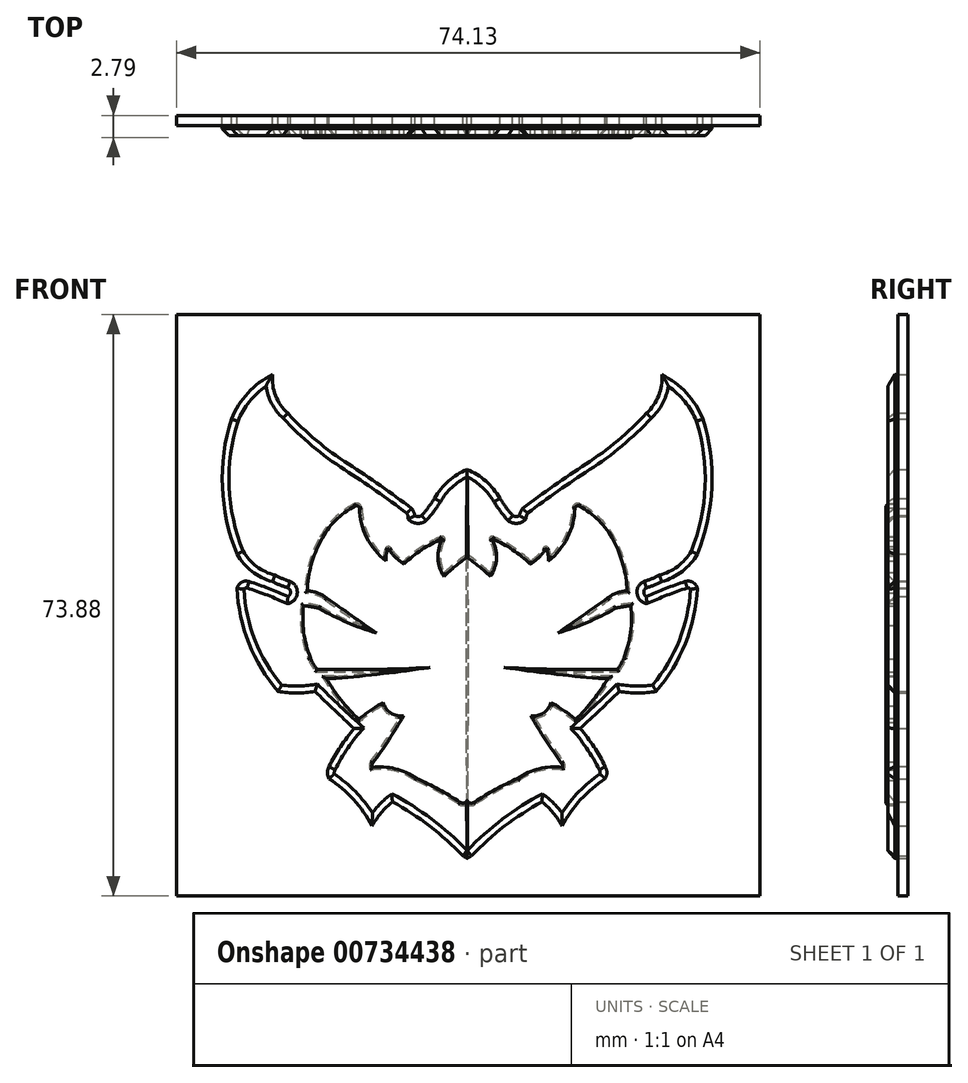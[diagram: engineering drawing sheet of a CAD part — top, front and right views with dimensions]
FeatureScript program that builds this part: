
annotation { "Feature Type Name" : "Feature", "Feature Type Description" : "" }
export const myFeature = defineFeature(function(context is Context, id is Id, definition is map)
    precondition{}
    {
        {
            var Q0;
            Q0=qCreatedBy(makeId("Front.planeOp"),FACE);
            var sketch = newSketch(context, id + "F0", { "sketchPlane" : qUnion([Q0])});
            skArc(sketch, "E0", {"start": v(0, 21.15) * mm, "mid": v(-2.37, 19.64) * mm, "end": v(-4.15, 17.47) * mm});
            skArc(sketch, "E1", {"start": v(-5.78, 15.28) * mm, "mid": v(-4.92, 16.34) * mm, "end": v(-4.15, 17.47) * mm});
            skArc(sketch, "E2", {"start": v(-6.65, 15.28) * mm, "mid": v(-6.22, 15.15) * mm, "end": v(-5.78, 15.28) * mm});
            skArc(sketch, "E3", {"start": v(-6.65, 15.28) * mm, "mid": v(-6.8, 15.75) * mm, "end": v(-7.04, 16.18) * mm});
            skArc(sketch, "E4", {"start": v(-7.04, 16.18) * mm, "mid": v(-11.01, 19.07) * mm, "end": v(-15.08, 21.83) * mm});
            skArc(sketch, "E5", {"start": v(-22.78, 28.28) * mm, "mid": v(-19.14, 24.8) * mm, "end": v(-15.08, 21.83) * mm});
            skArc(sketch, "E6", {"start": v(-24.73, 33.18) * mm, "mid": v(-24.33, 30.5) * mm, "end": v(-22.78, 28.28) * mm});
            skArc(sketch, "E7", {"start": v(-24.73, 33.18) * mm, "mid": v(-27.86, 30.85) * mm, "end": v(-29.94, 27.55) * mm});
            skArc(sketch, "E8", {"start": v(-29.94, 27.55) * mm, "mid": v(-31.1, 18.9) * mm, "end": v(-29.24, 10.37) * mm});
            skArc(sketch, "E9", {"start": v(-29.24, 10.37) * mm, "mid": v(-27.33, 8.18) * mm, "end": v(-24.73, 6.9) * mm});
            skArc(sketch, "E10", {"start": v(-24.73, 6.9) * mm, "mid": v(-23.77, 6.45) * mm, "end": v(-22.78, 6.1) * mm});
            skArc(sketch, "E11", {"start": v(-22.78, 5) * mm, "mid": v(-22.43, 5.55) * mm, "end": v(-22.78, 6.1) * mm});
            skArc(sketch, "E12", {"start": v(-22.78, 5) * mm, "mid": v(-25.2, 6.02) * mm, "end": v(-27.7, 6.9) * mm});
            skArc(sketch, "E13", {"start": v(-27.7, 6.9) * mm, "mid": v(-28.66, 6.8) * mm, "end": v(-29.24, 6.02) * mm});
            skPoint(sketch, "E13.endSnap0", {"position": v(-25.2, 6.02) * mm});
            skArc(sketch, "E14", {"start": v(-29.24, 6.02) * mm, "mid": v(-27.72, -0.96) * mm, "end": v(-24, -7.06) * mm});
            skArc(sketch, "E15", {"start": v(-24, -7.06) * mm, "mid": v(-21.67, -7.26) * mm, "end": v(-19.32, -7.06) * mm});
            skArc(sketch, "E16", {"start": v(-19.32, -7.06) * mm, "mid": v(-16.86, -9.44) * mm, "end": v(-14.34, -11.77) * mm});
            skArc(sketch, "E17", {"start": v(-14.34, -11.77) * mm, "mid": v(-16.1, -14.1) * mm, "end": v(-17.53, -16.62) * mm});
            skArc(sketch, "E18", {"start": v(-17.53, -16.62) * mm, "mid": v(-17.75, -17.38) * mm, "end": v(-17.53, -18.15) * mm});
            skArc(sketch, "E19", {"start": v(-12.06, -24.15) * mm, "mid": v(-14.43, -20.8) * mm, "end": v(-17.53, -18.15) * mm});
            skArc(sketch, "E20", {"start": v(-9.5, -21.1) * mm, "mid": v(-10.93, -22.5) * mm, "end": v(-12.06, -24.15) * mm});
            skArc(sketch, "E21", {"start": v(-0.55, -27.97) * mm, "mid": v(-4.75, -24.18) * mm, "end": v(-9.5, -21.1) * mm});
            skArc(sketch, "E22", {"start": v(0, -28.27) * mm, "mid": v(-0.27, -28.11) * mm, "end": v(-0.55, -27.97) * mm});
            skArc(sketch, "E23", {"start": v(0, 21.15) * mm, "mid": v(-0.15, -3.56) * mm, "end": v(0, -28.27) * mm});
            skSolve(sketch);
        }
        {
            var Q0;
            Q0 = qSketchRegion(id + "F0", true);
            extrude(context, id + "F1", {"entities" : qUnion([Q0]), "depth" : 2.54 * mm, "offsetDistance" : 25.4 * mm});
        }
        {
            var Q0;
            Q0=makeQuery(id+"F1.opExtrude","SWEPT_BODY",BODY,{"disambiguationData":[OSD([sQuery(id+"F0.wireOp",EDGE,"E0"),sQuery(id+"F0.wireOp",EDGE,"E1"),sQuery(id+"F0.wireOp",EDGE,"E2"),sQuery(id+"F0.wireOp",EDGE,"E3"),sQuery(id+"F0.wireOp",EDGE,"E4"),sQuery(id+"F0.wireOp",EDGE,"E5"),sQuery(id+"F0.wireOp",EDGE,"E6"),sQuery(id+"F0.wireOp",EDGE,"E7"),sQuery(id+"F0.wireOp",EDGE,"E8"),sQuery(id+"F0.wireOp",EDGE,"E9"),sQuery(id+"F0.wireOp",EDGE,"E10"),sQuery(id+"F0.wireOp",EDGE,"E11"),sQuery(id+"F0.wireOp",EDGE,"E12"),sQuery(id+"F0.wireOp",EDGE,"E13"),sQuery(id+"F0.wireOp",EDGE,"E14"),sQuery(id+"F0.wireOp",EDGE,"E15"),sQuery(id+"F0.wireOp",EDGE,"E16"),sQuery(id+"F0.wireOp",EDGE,"E17"),sQuery(id+"F0.wireOp",EDGE,"E18"),sQuery(id+"F0.wireOp",EDGE,"E19"),sQuery(id+"F0.wireOp",EDGE,"E20"),sQuery(id+"F0.wireOp",EDGE,"E21"),sQuery(id+"F0.wireOp",EDGE,"E22"),sQuery(id+"F0.wireOp",EDGE,"E23")])]});
            var Q1;
            Q1=qCreatedBy(makeId("Right.planeOp"),FACE);
            mirror(context, id + "F2", {"entities" : qUnion([Q0]), "mirrorPlane" : qUnion([Q1])});
        }
        {
            var Q0;
            Q0=qCreatedBy(makeId("Front.planeOp"),FACE);
            var sketch = newSketch(context, id + "F3", { "sketchPlane" : qUnion([Q0])});
            skLineSegment(sketch, "E24.bottom", {"start": v(-36.94, 40.82) * mm, "end": v(37.19, 40.82) * mm});
            skLineSegment(sketch, "E24.top", {"start": v(-36.94, -33.06) * mm, "end": v(37.19, -33.06) * mm});
            skLineSegment(sketch, "E24.left", {"start": v(-36.94, 40.82) * mm, "end": v(-36.94, -33.06) * mm});
            skLineSegment(sketch, "E24.right", {"start": v(37.19, 40.82) * mm, "end": v(37.19, -33.06) * mm});
            skSolve(sketch);
        }
        {
            var Q0;
            Q0 = qSketchRegion(id + "F3", true);
            extrude(context, id + "F4", {"entities" : qUnion([Q0]), "depth" : 1.27 * mm, "offsetDistance" : 25.4 * mm});
        }
        {
            var Q0;
            Q0=makeQuery(id+"F1.opExtrude","CAP_EDGE",EDGE,{"disambiguationData":[OSD([sQuery(id+"F0.wireOp",EDGE,"E4")])],"isStart":false});
            var Q1;
            Q1=makeQuery(id+"F1.opExtrude","CAP_EDGE",EDGE,{"disambiguationData":[OSD([sQuery(id+"F0.wireOp",EDGE,"E5")])],"isStart":false});
            var Q2;
            Q2=makeQuery(id+"F1.opExtrude","CAP_EDGE",EDGE,{"disambiguationData":[OSD([sQuery(id+"F0.wireOp",EDGE,"E6")])],"isStart":false});
            var Q3;
            Q3=makeQuery(id+"F1.opExtrude","CAP_EDGE",EDGE,{"disambiguationData":[OSD([sQuery(id+"F0.wireOp",EDGE,"E3")])],"isStart":false});
            var Q4;
            Q4=makeQuery(id+"F1.opExtrude","CAP_EDGE",EDGE,{"disambiguationData":[OSD([sQuery(id+"F0.wireOp",EDGE,"E2")])],"isStart":false});
            var Q5;
            Q5=makeQuery(id+"F1.opExtrude","CAP_EDGE",EDGE,{"disambiguationData":[OSD([sQuery(id+"F0.wireOp",EDGE,"E1")])],"isStart":false});
            var Q6;
            Q6=makeQuery(id+"F1.opExtrude","CAP_EDGE",EDGE,{"disambiguationData":[OSD([sQuery(id+"F0.wireOp",EDGE,"E0")])],"isStart":false});
            var Q7;
            Q7=makeQuery(id+"F2.opPattern","COPY",EDGE,{"derivedFrom":makeQuery(id+"F1.opExtrude","CAP_EDGE",EDGE,{"disambiguationData":[OSD([sQuery(id+"F0.wireOp",EDGE,"E0")])],"isStart":false}),"instanceName":"1"});
            var Q8;
            Q8=makeQuery(id+"F2.opPattern","COPY",EDGE,{"derivedFrom":makeQuery(id+"F1.opExtrude","CAP_EDGE",EDGE,{"disambiguationData":[OSD([sQuery(id+"F0.wireOp",EDGE,"E1")])],"isStart":false}),"instanceName":"1"});
            var Q9;
            Q9=makeQuery(id+"F2.opPattern","COPY",EDGE,{"derivedFrom":makeQuery(id+"F1.opExtrude","CAP_EDGE",EDGE,{"disambiguationData":[OSD([sQuery(id+"F0.wireOp",EDGE,"E2")])],"isStart":false}),"instanceName":"1"});
            var Q10;
            Q10=makeQuery(id+"F2.opPattern","COPY",EDGE,{"derivedFrom":makeQuery(id+"F1.opExtrude","CAP_EDGE",EDGE,{"disambiguationData":[OSD([sQuery(id+"F0.wireOp",EDGE,"E3")])],"isStart":false}),"instanceName":"1"});
            var Q11;
            Q11=makeQuery(id+"F2.opPattern","COPY",EDGE,{"derivedFrom":makeQuery(id+"F1.opExtrude","CAP_EDGE",EDGE,{"disambiguationData":[OSD([sQuery(id+"F0.wireOp",EDGE,"E4")])],"isStart":false}),"instanceName":"1"});
            var Q12;
            Q12=makeQuery(id+"F2.opPattern","COPY",EDGE,{"derivedFrom":makeQuery(id+"F1.opExtrude","CAP_EDGE",EDGE,{"disambiguationData":[OSD([sQuery(id+"F0.wireOp",EDGE,"E5")])],"isStart":false}),"instanceName":"1"});
            var Q13;
            Q13=makeQuery(id+"F2.opPattern","COPY",EDGE,{"derivedFrom":makeQuery(id+"F1.opExtrude","CAP_EDGE",EDGE,{"disambiguationData":[OSD([sQuery(id+"F0.wireOp",EDGE,"E6")])],"isStart":false}),"instanceName":"1"});
            var Q14;
            Q14=makeQuery(id+"F2.opPattern","COPY",EDGE,{"derivedFrom":makeQuery(id+"F1.opExtrude","CAP_EDGE",EDGE,{"disambiguationData":[OSD([sQuery(id+"F0.wireOp",EDGE,"E7")])],"isStart":false}),"instanceName":"1"});
            var Q15;
            Q15=makeQuery(id+"F2.opPattern","COPY",EDGE,{"derivedFrom":makeQuery(id+"F1.opExtrude","CAP_EDGE",EDGE,{"disambiguationData":[OSD([sQuery(id+"F0.wireOp",EDGE,"E8")])],"isStart":false}),"instanceName":"1"});
            var Q16;
            Q16=makeQuery(id+"F2.opPattern","COPY",EDGE,{"derivedFrom":makeQuery(id+"F1.opExtrude","CAP_EDGE",EDGE,{"disambiguationData":[OSD([sQuery(id+"F0.wireOp",EDGE,"E9")])],"isStart":false}),"instanceName":"1"});
            var Q17;
            Q17=makeQuery(id+"F2.opPattern","COPY",EDGE,{"derivedFrom":makeQuery(id+"F1.opExtrude","CAP_EDGE",EDGE,{"disambiguationData":[OSD([sQuery(id+"F0.wireOp",EDGE,"E10")])],"isStart":false}),"instanceName":"1"});
            var Q18;
            Q18=makeQuery(id+"F2.opPattern","COPY",EDGE,{"derivedFrom":makeQuery(id+"F1.opExtrude","CAP_EDGE",EDGE,{"disambiguationData":[OSD([sQuery(id+"F0.wireOp",EDGE,"E11")])],"isStart":false}),"instanceName":"1"});
            var Q19;
            Q19=makeQuery(id+"F2.opPattern","COPY",EDGE,{"derivedFrom":makeQuery(id+"F1.opExtrude","CAP_EDGE",EDGE,{"disambiguationData":[OSD([sQuery(id+"F0.wireOp",EDGE,"E12")])],"isStart":false}),"instanceName":"1"});
            var Q20;
            Q20=makeQuery(id+"F2.opPattern","COPY",EDGE,{"derivedFrom":makeQuery(id+"F1.opExtrude","CAP_EDGE",EDGE,{"disambiguationData":[OSD([sQuery(id+"F0.wireOp",EDGE,"E13")])],"isStart":false}),"instanceName":"1"});
            var Q21;
            Q21=makeQuery(id+"F2.opPattern","COPY",EDGE,{"derivedFrom":makeQuery(id+"F1.opExtrude","CAP_EDGE",EDGE,{"disambiguationData":[OSD([sQuery(id+"F0.wireOp",EDGE,"E14")])],"isStart":false}),"instanceName":"1"});
            var Q22;
            Q22=makeQuery(id+"F2.opPattern","COPY",EDGE,{"derivedFrom":makeQuery(id+"F1.opExtrude","CAP_EDGE",EDGE,{"disambiguationData":[OSD([sQuery(id+"F0.wireOp",EDGE,"E15")])],"isStart":false}),"instanceName":"1"});
            var Q23;
            Q23=makeQuery(id+"F2.opPattern","COPY",EDGE,{"derivedFrom":makeQuery(id+"F1.opExtrude","CAP_EDGE",EDGE,{"disambiguationData":[OSD([sQuery(id+"F0.wireOp",EDGE,"E16")])],"isStart":false}),"instanceName":"1"});
            var Q24;
            Q24=makeQuery(id+"F2.opPattern","COPY",EDGE,{"derivedFrom":makeQuery(id+"F1.opExtrude","CAP_EDGE",EDGE,{"disambiguationData":[OSD([sQuery(id+"F0.wireOp",EDGE,"E17")])],"isStart":false}),"instanceName":"1"});
            var Q25;
            Q25=makeQuery(id+"F2.opPattern","COPY",EDGE,{"derivedFrom":makeQuery(id+"F1.opExtrude","CAP_EDGE",EDGE,{"disambiguationData":[OSD([sQuery(id+"F0.wireOp",EDGE,"E18")])],"isStart":false}),"instanceName":"1"});
            var Q26;
            Q26=makeQuery(id+"F2.opPattern","COPY",EDGE,{"derivedFrom":makeQuery(id+"F1.opExtrude","CAP_EDGE",EDGE,{"disambiguationData":[OSD([sQuery(id+"F0.wireOp",EDGE,"E19")])],"isStart":false}),"instanceName":"1"});
            var Q27;
            Q27=makeQuery(id+"F2.opPattern","COPY",EDGE,{"derivedFrom":makeQuery(id+"F1.opExtrude","CAP_EDGE",EDGE,{"disambiguationData":[OSD([sQuery(id+"F0.wireOp",EDGE,"E20")])],"isStart":false}),"instanceName":"1"});
            var Q28;
            Q28=makeQuery(id+"F2.opPattern","COPY",EDGE,{"derivedFrom":makeQuery(id+"F1.opExtrude","CAP_EDGE",EDGE,{"disambiguationData":[OSD([sQuery(id+"F0.wireOp",EDGE,"E21")])],"isStart":false}),"instanceName":"1"});
            var Q29;
            Q29=makeQuery(id+"F2.opPattern","COPY",EDGE,{"derivedFrom":makeQuery(id+"F1.opExtrude","CAP_EDGE",EDGE,{"disambiguationData":[OSD([sQuery(id+"F0.wireOp",EDGE,"E22")])],"isStart":false}),"instanceName":"1"});
            var Q30;
            Q30=makeQuery(id+"F1.opExtrude","CAP_EDGE",EDGE,{"disambiguationData":[OSD([sQuery(id+"F0.wireOp",EDGE,"E22")])],"isStart":false});
            var Q31;
            Q31=makeQuery(id+"F1.opExtrude","CAP_EDGE",EDGE,{"disambiguationData":[OSD([sQuery(id+"F0.wireOp",EDGE,"E21")])],"isStart":false});
            var Q32;
            Q32=makeQuery(id+"F1.opExtrude","CAP_EDGE",EDGE,{"disambiguationData":[OSD([sQuery(id+"F0.wireOp",EDGE,"E20")])],"isStart":false});
            var Q33;
            Q33=makeQuery(id+"F1.opExtrude","CAP_EDGE",EDGE,{"disambiguationData":[OSD([sQuery(id+"F0.wireOp",EDGE,"E19")])],"isStart":false});
            var Q34;
            Q34=makeQuery(id+"F1.opExtrude","CAP_EDGE",EDGE,{"disambiguationData":[OSD([sQuery(id+"F0.wireOp",EDGE,"E18")])],"isStart":false});
            var Q35;
            Q35=makeQuery(id+"F1.opExtrude","CAP_EDGE",EDGE,{"disambiguationData":[OSD([sQuery(id+"F0.wireOp",EDGE,"E17")])],"isStart":false});
            var Q36;
            Q36=makeQuery(id+"F1.opExtrude","CAP_EDGE",EDGE,{"disambiguationData":[OSD([sQuery(id+"F0.wireOp",EDGE,"E16")])],"isStart":false});
            var Q37;
            Q37=makeQuery(id+"F1.opExtrude","CAP_EDGE",EDGE,{"disambiguationData":[OSD([sQuery(id+"F0.wireOp",EDGE,"E15")])],"isStart":false});
            var Q38;
            Q38=makeQuery(id+"F1.opExtrude","CAP_EDGE",EDGE,{"disambiguationData":[OSD([sQuery(id+"F0.wireOp",EDGE,"E14")])],"isStart":false});
            var Q39;
            Q39=makeQuery(id+"F1.opExtrude","CAP_EDGE",EDGE,{"disambiguationData":[OSD([sQuery(id+"F0.wireOp",EDGE,"E13")])],"isStart":false});
            var Q40;
            Q40=makeQuery(id+"F1.opExtrude","CAP_EDGE",EDGE,{"disambiguationData":[OSD([sQuery(id+"F0.wireOp",EDGE,"E12")])],"isStart":false});
            var Q41;
            Q41=makeQuery(id+"F1.opExtrude","CAP_EDGE",EDGE,{"disambiguationData":[OSD([sQuery(id+"F0.wireOp",EDGE,"E11")])],"isStart":false});
            var Q42;
            Q42=makeQuery(id+"F1.opExtrude","CAP_EDGE",EDGE,{"disambiguationData":[OSD([sQuery(id+"F0.wireOp",EDGE,"E10")])],"isStart":false});
            var Q43;
            Q43=makeQuery(id+"F1.opExtrude","CAP_EDGE",EDGE,{"disambiguationData":[OSD([sQuery(id+"F0.wireOp",EDGE,"E9")])],"isStart":false});
            var Q44;
            Q44=makeQuery(id+"F1.opExtrude","CAP_EDGE",EDGE,{"disambiguationData":[OSD([sQuery(id+"F0.wireOp",EDGE,"E8")])],"isStart":false});
            var Q45;
            Q45=makeQuery(id+"F1.opExtrude","CAP_EDGE",EDGE,{"disambiguationData":[OSD([sQuery(id+"F0.wireOp",EDGE,"E7")])],"isStart":false});
            chamfer(context, id + "F5", {"entities" : qUnion([Q0, Q1, Q2, Q3, Q4, Q5, Q6, Q7, Q8, Q9, Q10, Q11, Q12, Q13, Q14, Q15, Q16, Q17, Q18, Q19, Q20, Q21, Q22, Q23, Q24, Q25, Q26, Q27, Q28, Q29, Q30, Q31, Q32, Q33, Q34, Q35, Q36, Q37, Q38, Q39, Q40, Q41, Q42, Q43, Q44, Q45]), "width" : 0.86 * mm, "tangentPropagation" : true});
        }
        {
            var Q0;
            Q0=makeQuery(id+"F4.opExtrude","CAP_FACE",FACE,{"disambiguationData":[OSD([sQuery(id+"F3.wireOp",EDGE,"E24.bottom"),sQuery(id+"F3.wireOp",EDGE,"E24.top"),sQuery(id+"F3.wireOp",EDGE,"E24.left"),sQuery(id+"F3.wireOp",EDGE,"E24.right")])],"isStart":false});
            var sketch = newSketch(context, id + "F6", { "sketchPlane" : qUnion([Q0])});
            skArc(sketch, "E25", {"start": v(0, 10.33) * mm, "mid": v(-1.49, 9.24) * mm, "end": v(-2.88, 8.03) * mm});
            skArc(sketch, "E26", {"start": v(-2.88, 12.09) * mm, "mid": v(-3.42, 10.06) * mm, "end": v(-2.88, 8.03) * mm});
            skArc(sketch, "E27", {"start": v(-2.88, 12.09) * mm, "mid": v(-2.95, 12.56) * mm, "end": v(-3.42, 12.56) * mm});
            skPoint(sketch, "E27.endSnap0", {"position": v(-3.42, 10.06) * mm});
            skArc(sketch, "E28", {"start": v(-3.42, 12.56) * mm, "mid": v(-5.87, 11.24) * mm, "end": v(-8.05, 9.5) * mm});
            skArc(sketch, "E29", {"start": v(-9.61, 11.03) * mm, "mid": v(-8.9, 10.2) * mm, "end": v(-8.05, 9.5) * mm});
            skArc(sketch, "E30", {"start": v(-9.61, 11.03) * mm, "mid": v(-10, 11.33) * mm, "end": v(-10.4, 11.03) * mm});
            skArc(sketch, "E31", {"start": v(-10.4, 11.03) * mm, "mid": v(-10.53, 10.6) * mm, "end": v(-10.61, 10.16) * mm});
            skArc(sketch, "E32", {"start": v(-13.38, 16.22) * mm, "mid": v(-12.62, 12.9) * mm, "end": v(-10.61, 10.16) * mm});
            skArc(sketch, "E33", {"start": v(-13.38, 16.22) * mm, "mid": v(-13.73, 16.75) * mm, "end": v(-14.36, 16.76) * mm});
            skArc(sketch, "E34", {"start": v(-14.36, 16.76) * mm, "mid": v(-16.95, 14.86) * mm, "end": v(-18.86, 12.26) * mm});
            skArc(sketch, "E35", {"start": v(-18.86, 12.26) * mm, "mid": v(-20.14, 8.94) * mm, "end": v(-20.62, 5.42) * mm});
            skArc(sketch, "E36", {"start": v(-18.02, 4.55) * mm, "mid": v(-19.25, 5.2) * mm, "end": v(-20.62, 5.42) * mm});
            skArc(sketch, "E37", {"start": v(-18.02, 4.55) * mm, "mid": v(-15.7, 2.92) * mm, "end": v(-13.38, 1.3) * mm});
            skArc(sketch, "E38", {"start": v(-18.69, 3.77) * mm, "mid": v(-16.09, 2.41) * mm, "end": v(-13.38, 1.3) * mm});
            skArc(sketch, "E39", {"start": v(-18.69, 3.77) * mm, "mid": v(-19.86, 4.02) * mm, "end": v(-21.05, 4.14) * mm});
            skArc(sketch, "E40", {"start": v(-21.05, 4.14) * mm, "mid": v(-21.08, 0.55) * mm, "end": v(-20.19, -2.92) * mm});
            skArc(sketch, "E41", {"start": v(-20.19, -2.92) * mm, "mid": v(-19.78, -3.78) * mm, "end": v(-19.24, -4.56) * mm});
            skArc(sketch, "E42", {"start": v(-19.24, -4.56) * mm, "mid": v(-15.22, -4.6) * mm, "end": v(-11.2, -4.56) * mm});
            skArc(sketch, "E43", {"start": v(-16.67, -5.14) * mm, "mid": v(-13.94, -4.86) * mm, "end": v(-11.2, -4.56) * mm});
            skArc(sketch, "E44", {"start": v(-16.67, -5.14) * mm, "mid": v(-17.55, -5.1) * mm, "end": v(-18.44, -5.14) * mm});
            skArc(sketch, "E45", {"start": v(-18.44, -5.14) * mm, "mid": v(-16.32, -8.24) * mm, "end": v(-13.8, -11.02) * mm});
            skArc(sketch, "E46", {"start": v(-10.83, -8.9) * mm, "mid": v(-12.35, -9.9) * mm, "end": v(-13.8, -11.02) * mm});
            skArc(sketch, "E47", {"start": v(-10.83, -8.9) * mm, "mid": v(-9.94, -10) * mm, "end": v(-8.61, -10.48) * mm});
            skArc(sketch, "E48", {"start": v(-12.26, -16) * mm, "mid": v(-10.36, -13.29) * mm, "end": v(-8.61, -10.48) * mm});
            skArc(sketch, "E49", {"start": v(-12.26, -16) * mm, "mid": v(-12.43, -16.53) * mm, "end": v(-12.26, -17.06) * mm});
            skArc(sketch, "E50", {"start": v(-6.62, -18.37) * mm, "mid": v(-9.3, -17.15) * mm, "end": v(-12.26, -17.06) * mm});
            skArc(sketch, "E51", {"start": v(-1.07, -21.38) * mm, "mid": v(-3.79, -19.78) * mm, "end": v(-6.62, -18.37) * mm});
            skArc(sketch, "E52", {"start": v(-1.07, -21.38) * mm, "mid": v(-0.54, -21.57) * mm, "end": v(0, -21.38) * mm});
            skArc(sketch, "E53", {"start": v(0, 10.33) * mm, "mid": v(-0.06, -5.53) * mm, "end": v(0, -21.38) * mm});
            skArc(sketch, "E54.MirrorCS", {"start": v(10.4, 11.03) * mm, "mid": v(10.53, 10.6) * mm, "end": v(10.61, 10.16) * mm});
            skArc(sketch, "E55.MirrorCS", {"start": v(2.88, 12.09) * mm, "mid": v(2.95, 12.56) * mm, "end": v(3.42, 12.56) * mm});
            skArc(sketch, "E56.MirrorCS", {"start": v(9.61, 11.03) * mm, "mid": v(10, 11.33) * mm, "end": v(10.4, 11.03) * mm});
            skArc(sketch, "E57.MirrorCS", {"start": v(18.69, 3.77) * mm, "mid": v(19.86, 4.02) * mm, "end": v(21.05, 4.14) * mm});
            skArc(sketch, "E58.MirrorCS", {"start": v(16.67, -5.14) * mm, "mid": v(17.55, -5.1) * mm, "end": v(18.44, -5.14) * mm});
            skArc(sketch, "E59.MirrorCS", {"start": v(10.83, -8.9) * mm, "mid": v(12.35, -9.9) * mm, "end": v(13.8, -11.02) * mm});
            skArc(sketch, "E60.MirrorCS", {"start": v(18.02, 4.55) * mm, "mid": v(19.25, 5.2) * mm, "end": v(20.62, 5.42) * mm});
            skArc(sketch, "E61.MirrorCS", {"start": v(20.19, -2.92) * mm, "mid": v(19.78, -3.78) * mm, "end": v(19.24, -4.56) * mm});
            skArc(sketch, "E62.MirrorCS", {"start": v(12.26, -16) * mm, "mid": v(12.43, -16.53) * mm, "end": v(12.26, -17.06) * mm});
            skArc(sketch, "E63.MirrorCS", {"start": v(1.07, -21.38) * mm, "mid": v(0.54, -21.57) * mm, "end": v(0, -21.38) * mm});
            skArc(sketch, "E64.MirrorCS", {"start": v(13.38, 16.22) * mm, "mid": v(13.73, 16.75) * mm, "end": v(14.36, 16.76) * mm});
            skArc(sketch, "E65.MirrorCS", {"start": v(9.61, 11.03) * mm, "mid": v(8.9, 10.2) * mm, "end": v(8.05, 9.5) * mm});
            skArc(sketch, "E66.MirrorCS", {"start": v(10.83, -8.9) * mm, "mid": v(9.94, -10) * mm, "end": v(8.61, -10.48) * mm});
            skArc(sketch, "E67.MirrorCS", {"start": v(2.88, 12.09) * mm, "mid": v(3.42, 10.06) * mm, "end": v(2.88, 8.03) * mm});
            skArc(sketch, "E68.MirrorCS", {"start": v(1.07, -21.38) * mm, "mid": v(3.79, -19.78) * mm, "end": v(6.62, -18.37) * mm});
            skArc(sketch, "E69.MirrorCS", {"start": v(18.69, 3.77) * mm, "mid": v(16.09, 2.41) * mm, "end": v(13.38, 1.3) * mm});
            skArc(sketch, "E70.MirrorCS", {"start": v(21.05, 4.14) * mm, "mid": v(21.08, 0.55) * mm, "end": v(20.19, -2.92) * mm});
            skArc(sketch, "E71.MirrorCS", {"start": v(6.62, -18.37) * mm, "mid": v(9.3, -17.15) * mm, "end": v(12.26, -17.06) * mm});
            skArc(sketch, "E72.MirrorCS", {"start": v(0, 10.33) * mm, "mid": v(1.49, 9.24) * mm, "end": v(2.88, 8.03) * mm});
            skArc(sketch, "E73.MirrorCS", {"start": v(18.02, 4.55) * mm, "mid": v(15.7, 2.92) * mm, "end": v(13.38, 1.3) * mm});
            skPoint(sketch, "E74.MirrorP", {"position": v(3.42, 10.06) * mm});
            skArc(sketch, "E75.MirrorCS", {"start": v(18.86, 12.26) * mm, "mid": v(20.14, 8.94) * mm, "end": v(20.62, 5.42) * mm});
            skArc(sketch, "E76.MirrorCS", {"start": v(0, 10.33) * mm, "mid": v(0.06, -5.53) * mm, "end": v(0, -21.38) * mm});
            skArc(sketch, "E77.MirrorCS", {"start": v(13.38, 16.22) * mm, "mid": v(12.62, 12.9) * mm, "end": v(10.61, 10.16) * mm});
            skArc(sketch, "E78.MirrorCS", {"start": v(19.24, -4.56) * mm, "mid": v(15.22, -4.6) * mm, "end": v(11.2, -4.56) * mm});
            skArc(sketch, "E79.MirrorCS", {"start": v(3.42, 12.56) * mm, "mid": v(5.87, 11.24) * mm, "end": v(8.05, 9.5) * mm});
            skArc(sketch, "E80.MirrorCS", {"start": v(14.36, 16.76) * mm, "mid": v(16.95, 14.86) * mm, "end": v(18.86, 12.26) * mm});
            skArc(sketch, "E81.MirrorCS", {"start": v(12.26, -16) * mm, "mid": v(10.36, -13.29) * mm, "end": v(8.61, -10.48) * mm});
            skArc(sketch, "E82.MirrorCS", {"start": v(16.67, -5.14) * mm, "mid": v(13.94, -4.86) * mm, "end": v(11.2, -4.56) * mm});
            skArc(sketch, "E83.MirrorCS", {"start": v(18.44, -5.14) * mm, "mid": v(16.32, -8.24) * mm, "end": v(13.8, -11.02) * mm});
            skSolve(sketch);
        }
        {
            var Q0;
            Q0 = qSketchRegion(id + "F6", true);
            extrude(context, id + "F7", {"entities" : qUnion([Q0]), "depth" : 1.52 * mm, "offsetDistance" : 25.4 * mm});
        }
        {
            var Q0;
            Q0=makeQuery(id+"F7.opExtrude","CAP_EDGE",EDGE,{"disambiguationData":[OSD([sQuery(id+"F6.wireOp",EDGE,"E34")])],"isStart":false});
            var Q1;
            Q1=makeQuery(id+"F7.opExtrude","CAP_EDGE",EDGE,{"disambiguationData":[OSD([sQuery(id+"F6.wireOp",EDGE,"E33")])],"isStart":false});
            var Q2;
            Q2=makeQuery(id+"F7.opExtrude","CAP_EDGE",EDGE,{"disambiguationData":[OSD([sQuery(id+"F6.wireOp",EDGE,"E32")])],"isStart":false});
            var Q3;
            Q3=makeQuery(id+"F7.opExtrude","CAP_EDGE",EDGE,{"disambiguationData":[OSD([sQuery(id+"F6.wireOp",EDGE,"E31")])],"isStart":false});
            var Q4;
            Q4=makeQuery(id+"F7.opExtrude","CAP_EDGE",EDGE,{"disambiguationData":[OSD([sQuery(id+"F6.wireOp",EDGE,"E30")])],"isStart":false});
            var Q5;
            Q5=makeQuery(id+"F7.opExtrude","CAP_EDGE",EDGE,{"disambiguationData":[OSD([sQuery(id+"F6.wireOp",EDGE,"E29")])],"isStart":false});
            var Q6;
            Q6=makeQuery(id+"F7.opExtrude","CAP_EDGE",EDGE,{"disambiguationData":[OSD([sQuery(id+"F6.wireOp",EDGE,"E28")])],"isStart":false});
            var Q7;
            Q7=makeQuery(id+"F7.opExtrude","CAP_EDGE",EDGE,{"disambiguationData":[OSD([sQuery(id+"F6.wireOp",EDGE,"E26")])],"isStart":false});
            var Q8;
            Q8=makeQuery(id+"F7.opExtrude","CAP_EDGE",EDGE,{"disambiguationData":[OSD([sQuery(id+"F6.wireOp",EDGE,"E27")])],"isStart":false});
            var Q9;
            Q9=makeQuery(id+"F7.opExtrude","CAP_EDGE",EDGE,{"disambiguationData":[OSD([sQuery(id+"F6.wireOp",EDGE,"E25")])],"isStart":false});
            var Q10;
            Q10=makeQuery(id+"F7.opExtrude","CAP_EDGE",EDGE,{"disambiguationData":[OSD([sQuery(id+"F6.wireOp",EDGE,"E72.MirrorCS")])],"isStart":false});
            var Q11;
            Q11=makeQuery(id+"F7.opExtrude","CAP_EDGE",EDGE,{"disambiguationData":[OSD([sQuery(id+"F6.wireOp",EDGE,"E67.MirrorCS")])],"isStart":false});
            var Q12;
            Q12=makeQuery(id+"F7.opExtrude","CAP_EDGE",EDGE,{"disambiguationData":[OSD([sQuery(id+"F6.wireOp",EDGE,"E55.MirrorCS")])],"isStart":false});
            var Q13;
            Q13=makeQuery(id+"F7.opExtrude","CAP_EDGE",EDGE,{"disambiguationData":[OSD([sQuery(id+"F6.wireOp",EDGE,"E79.MirrorCS")])],"isStart":false});
            var Q14;
            Q14=makeQuery(id+"F7.opExtrude","CAP_EDGE",EDGE,{"disambiguationData":[OSD([sQuery(id+"F6.wireOp",EDGE,"E65.MirrorCS")])],"isStart":false});
            var Q15;
            Q15=makeQuery(id+"F7.opExtrude","CAP_EDGE",EDGE,{"disambiguationData":[OSD([sQuery(id+"F6.wireOp",EDGE,"E56.MirrorCS")])],"isStart":false});
            var Q16;
            Q16=makeQuery(id+"F7.opExtrude","CAP_EDGE",EDGE,{"disambiguationData":[OSD([sQuery(id+"F6.wireOp",EDGE,"E54.MirrorCS")])],"isStart":false});
            var Q17;
            Q17=makeQuery(id+"F7.opExtrude","CAP_EDGE",EDGE,{"disambiguationData":[OSD([sQuery(id+"F6.wireOp",EDGE,"E77.MirrorCS")])],"isStart":false});
            var Q18;
            Q18=makeQuery(id+"F7.opExtrude","CAP_EDGE",EDGE,{"disambiguationData":[OSD([sQuery(id+"F6.wireOp",EDGE,"E64.MirrorCS")])],"isStart":false});
            var Q19;
            Q19=makeQuery(id+"F7.opExtrude","CAP_EDGE",EDGE,{"disambiguationData":[OSD([sQuery(id+"F6.wireOp",EDGE,"E80.MirrorCS")])],"isStart":false});
            var Q20;
            Q20=makeQuery(id+"F7.opExtrude","CAP_EDGE",EDGE,{"disambiguationData":[OSD([sQuery(id+"F6.wireOp",EDGE,"E75.MirrorCS")])],"isStart":false});
            var Q21;
            Q21=makeQuery(id+"F7.opExtrude","CAP_EDGE",EDGE,{"disambiguationData":[OSD([sQuery(id+"F6.wireOp",EDGE,"E60.MirrorCS")])],"isStart":false});
            var Q22;
            Q22=makeQuery(id+"F7.opExtrude","CAP_EDGE",EDGE,{"disambiguationData":[OSD([sQuery(id+"F6.wireOp",EDGE,"E73.MirrorCS")])],"isStart":false});
            var Q23;
            Q23=makeQuery(id+"F7.opExtrude","CAP_EDGE",EDGE,{"disambiguationData":[OSD([sQuery(id+"F6.wireOp",EDGE,"E69.MirrorCS")])],"isStart":false});
            var Q24;
            Q24=makeQuery(id+"F7.opExtrude","CAP_EDGE",EDGE,{"disambiguationData":[OSD([sQuery(id+"F6.wireOp",EDGE,"E57.MirrorCS")])],"isStart":false});
            var Q25;
            Q25=makeQuery(id+"F7.opExtrude","CAP_EDGE",EDGE,{"disambiguationData":[OSD([sQuery(id+"F6.wireOp",EDGE,"E70.MirrorCS")])],"isStart":false});
            var Q26;
            Q26=makeQuery(id+"F7.opExtrude","CAP_EDGE",EDGE,{"disambiguationData":[OSD([sQuery(id+"F6.wireOp",EDGE,"E61.MirrorCS")])],"isStart":false});
            var Q27;
            Q27=makeQuery(id+"F7.opExtrude","CAP_EDGE",EDGE,{"disambiguationData":[OSD([sQuery(id+"F6.wireOp",EDGE,"E78.MirrorCS")])],"isStart":false});
            var Q28;
            Q28=makeQuery(id+"F7.opExtrude","CAP_EDGE",EDGE,{"disambiguationData":[OSD([sQuery(id+"F6.wireOp",EDGE,"E82.MirrorCS")])],"isStart":false});
            var Q29;
            Q29=makeQuery(id+"F7.opExtrude","CAP_EDGE",EDGE,{"disambiguationData":[OSD([sQuery(id+"F6.wireOp",EDGE,"E58.MirrorCS")])],"isStart":false});
            var Q30;
            Q30=makeQuery(id+"F7.opExtrude","CAP_EDGE",EDGE,{"disambiguationData":[OSD([sQuery(id+"F6.wireOp",EDGE,"E83.MirrorCS")])],"isStart":false});
            var Q31;
            Q31=makeQuery(id+"F7.opExtrude","CAP_EDGE",EDGE,{"disambiguationData":[OSD([sQuery(id+"F6.wireOp",EDGE,"E59.MirrorCS")])],"isStart":false});
            var Q32;
            Q32=makeQuery(id+"F7.opExtrude","CAP_EDGE",EDGE,{"disambiguationData":[OSD([sQuery(id+"F6.wireOp",EDGE,"E66.MirrorCS")])],"isStart":false});
            var Q33;
            Q33=makeQuery(id+"F7.opExtrude","CAP_EDGE",EDGE,{"disambiguationData":[OSD([sQuery(id+"F6.wireOp",EDGE,"E81.MirrorCS")])],"isStart":false});
            var Q34;
            Q34=makeQuery(id+"F7.opExtrude","CAP_EDGE",EDGE,{"disambiguationData":[OSD([sQuery(id+"F6.wireOp",EDGE,"E62.MirrorCS")])],"isStart":false});
            var Q35;
            Q35=makeQuery(id+"F7.opExtrude","CAP_EDGE",EDGE,{"disambiguationData":[OSD([sQuery(id+"F6.wireOp",EDGE,"E71.MirrorCS")])],"isStart":false});
            var Q36;
            Q36=makeQuery(id+"F7.opExtrude","CAP_EDGE",EDGE,{"disambiguationData":[OSD([sQuery(id+"F6.wireOp",EDGE,"E68.MirrorCS")])],"isStart":false});
            var Q37;
            Q37=makeQuery(id+"F7.opExtrude","CAP_EDGE",EDGE,{"disambiguationData":[OSD([sQuery(id+"F6.wireOp",EDGE,"E63.MirrorCS")])],"isStart":false});
            var Q38;
            Q38=makeQuery(id+"F7.opExtrude","CAP_EDGE",EDGE,{"disambiguationData":[OSD([sQuery(id+"F6.wireOp",EDGE,"E52")])],"isStart":false});
            var Q39;
            Q39=makeQuery(id+"F7.opExtrude","CAP_EDGE",EDGE,{"disambiguationData":[OSD([sQuery(id+"F6.wireOp",EDGE,"E51")])],"isStart":false});
            var Q40;
            Q40=makeQuery(id+"F7.opExtrude","CAP_EDGE",EDGE,{"disambiguationData":[OSD([sQuery(id+"F6.wireOp",EDGE,"E50")])],"isStart":false});
            var Q41;
            Q41=makeQuery(id+"F7.opExtrude","CAP_EDGE",EDGE,{"disambiguationData":[OSD([sQuery(id+"F6.wireOp",EDGE,"E49")])],"isStart":false});
            var Q42;
            Q42=makeQuery(id+"F7.opExtrude","CAP_EDGE",EDGE,{"disambiguationData":[OSD([sQuery(id+"F6.wireOp",EDGE,"E48")])],"isStart":false});
            var Q43;
            Q43=makeQuery(id+"F7.opExtrude","CAP_EDGE",EDGE,{"disambiguationData":[OSD([sQuery(id+"F6.wireOp",EDGE,"E47")])],"isStart":false});
            var Q44;
            Q44=makeQuery(id+"F7.opExtrude","CAP_EDGE",EDGE,{"disambiguationData":[OSD([sQuery(id+"F6.wireOp",EDGE,"E46")])],"isStart":false});
            var Q45;
            Q45=makeQuery(id+"F7.opExtrude","CAP_EDGE",EDGE,{"disambiguationData":[OSD([sQuery(id+"F6.wireOp",EDGE,"E45")])],"isStart":false});
            var Q46;
            Q46=makeQuery(id+"F7.opExtrude","CAP_EDGE",EDGE,{"disambiguationData":[OSD([sQuery(id+"F6.wireOp",EDGE,"E44")])],"isStart":false});
            var Q47;
            Q47=makeQuery(id+"F7.opExtrude","CAP_EDGE",EDGE,{"disambiguationData":[OSD([sQuery(id+"F6.wireOp",EDGE,"E43")])],"isStart":false});
            var Q48;
            Q48=makeQuery(id+"F7.opExtrude","CAP_EDGE",EDGE,{"disambiguationData":[OSD([sQuery(id+"F6.wireOp",EDGE,"E42")])],"isStart":false});
            var Q49;
            Q49=makeQuery(id+"F7.opExtrude","CAP_EDGE",EDGE,{"disambiguationData":[OSD([sQuery(id+"F6.wireOp",EDGE,"E41")])],"isStart":false});
            var Q50;
            Q50=makeQuery(id+"F7.opExtrude","CAP_EDGE",EDGE,{"disambiguationData":[OSD([sQuery(id+"F6.wireOp",EDGE,"E40")])],"isStart":false});
            var Q51;
            Q51=makeQuery(id+"F7.opExtrude","CAP_EDGE",EDGE,{"disambiguationData":[OSD([sQuery(id+"F6.wireOp",EDGE,"E39")])],"isStart":false});
            var Q52;
            Q52=makeQuery(id+"F7.opExtrude","CAP_EDGE",EDGE,{"disambiguationData":[OSD([sQuery(id+"F6.wireOp",EDGE,"E38")])],"isStart":false});
            var Q53;
            Q53=makeQuery(id+"F7.opExtrude","CAP_EDGE",EDGE,{"disambiguationData":[OSD([sQuery(id+"F6.wireOp",EDGE,"E37")])],"isStart":false});
            var Q54;
            Q54=makeQuery(id+"F7.opExtrude","CAP_EDGE",EDGE,{"disambiguationData":[OSD([sQuery(id+"F6.wireOp",EDGE,"E36")])],"isStart":false});
            var Q55;
            Q55=makeQuery(id+"F7.opExtrude","CAP_EDGE",EDGE,{"disambiguationData":[OSD([sQuery(id+"F6.wireOp",EDGE,"E35")])],"isStart":false});
            chamfer(context, id + "F8", {"entities" : qUnion([Q0, Q1, Q2, Q3, Q4, Q5, Q6, Q7, Q8, Q9, Q10, Q11, Q12, Q13, Q14, Q15, Q16, Q17, Q18, Q19, Q20, Q21, Q22, Q23, Q24, Q25, Q26, Q27, Q28, Q29, Q30, Q31, Q32, Q33, Q34, Q35, Q36, Q37, Q38, Q39, Q40, Q41, Q42, Q43, Q44, Q45, Q46, Q47, Q48, Q49, Q50, Q51, Q52, Q53, Q54, Q55]), "width" : 0.3 * mm, "tangentPropagation" : true});
        }
    });
